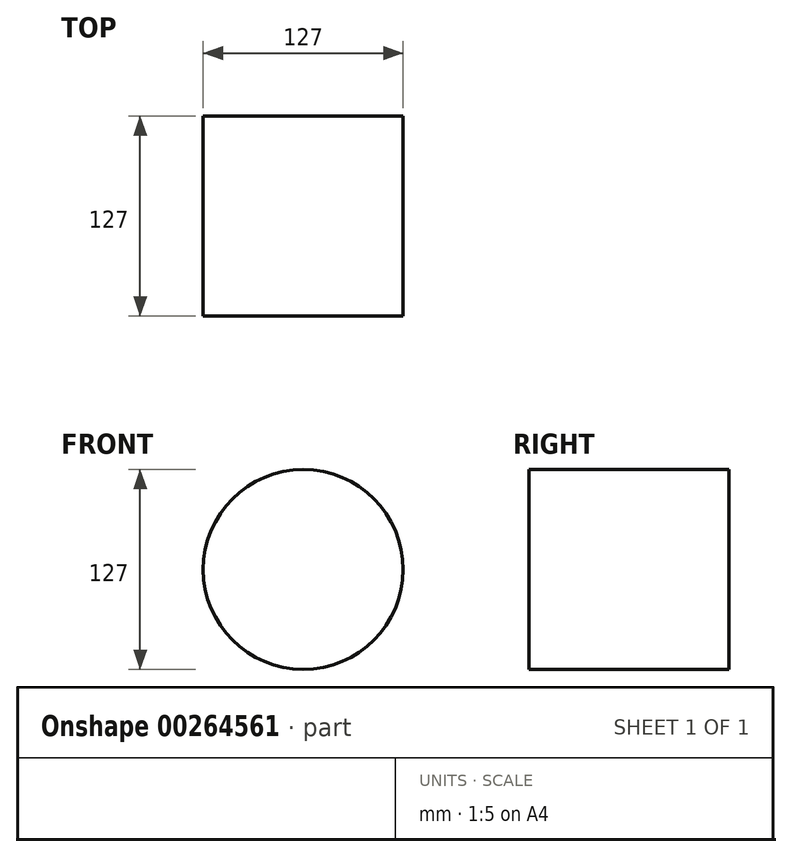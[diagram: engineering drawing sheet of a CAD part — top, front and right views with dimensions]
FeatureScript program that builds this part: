
annotation { "Feature Type Name" : "Feature", "Feature Type Description" : "" }
export const myFeature = defineFeature(function(context is Context, id is Id, definition is map)
    precondition{}
    {
        {
            var Q0;
            Q0=qCreatedBy(makeId("Front.planeOp"),FACE);
            var sketch = newSketch(context, id + "F0", { "sketchPlane" : qUnion([Q0])});
            skCircle(sketch, "E0", {"center": v(0, 0) * mm, "radius": 63.5 * mm});
            skSolve(sketch);
        }
        {
            var Q0;
            Q0 = qSketchRegion(id + "F0", true);
            extrude(context, id + "F1", {"entities" : qUnion([Q0]), "oppositeDirection" : true, "depth" : 127 * mm});
        }
    });
